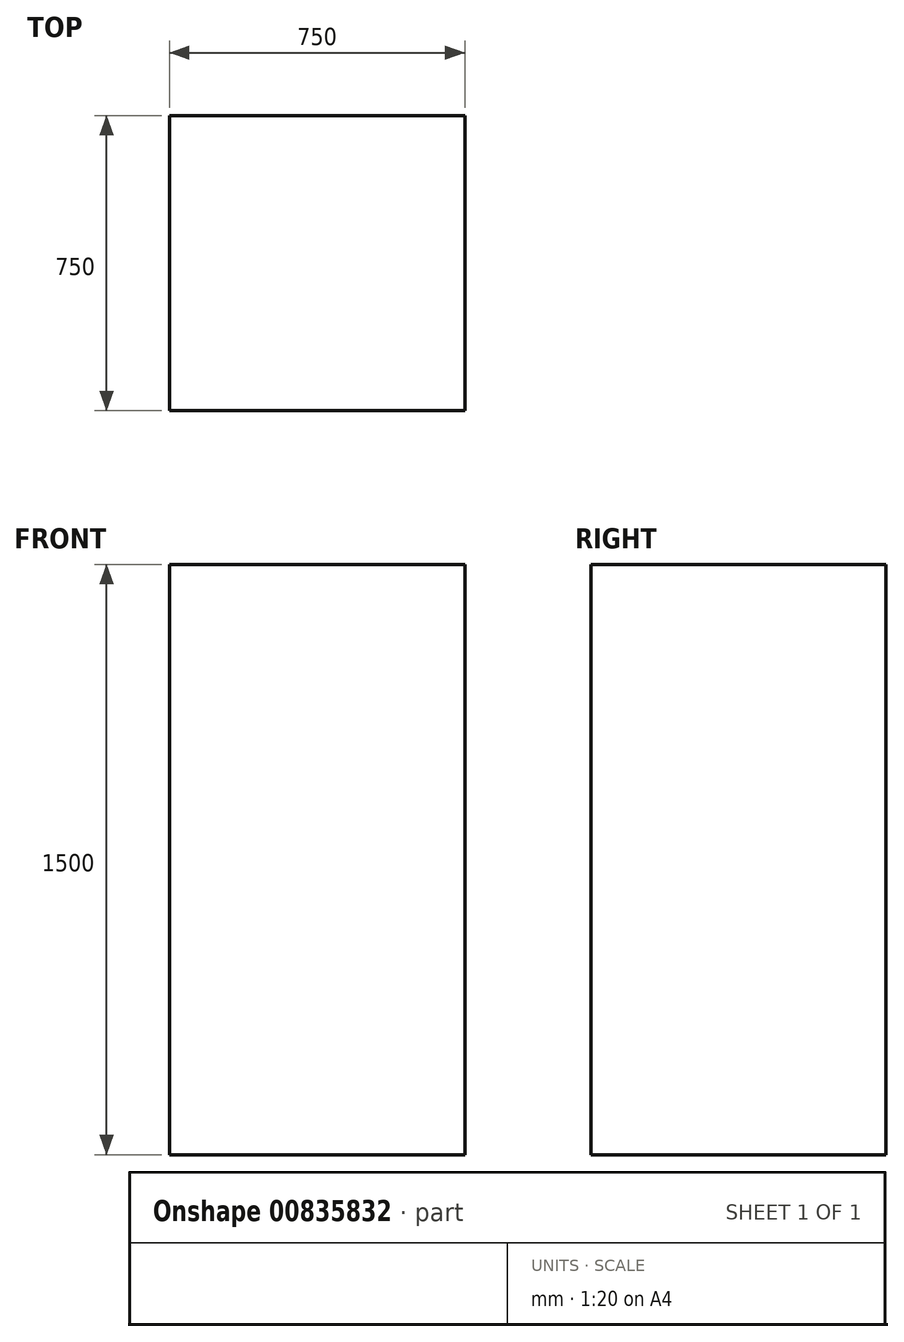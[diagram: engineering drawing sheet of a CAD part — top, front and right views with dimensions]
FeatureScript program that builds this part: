
annotation { "Feature Type Name" : "Feature", "Feature Type Description" : "" }
export const myFeature = defineFeature(function(context is Context, id is Id, definition is map)
    precondition{}
    {
        {
            var Q0;
            Q0=qCreatedBy(makeId("Top.planeOp"),FACE);
            var sketch = newSketch(context, id + "F0", { "sketchPlane" : qUnion([Q0])});
            skLineSegment(sketch, "E0.bottom", {"start": v(-375, 375) * mm, "end": v(375, 375) * mm});
            skLineSegment(sketch, "E0.top", {"start": v(-375, -375) * mm, "end": v(375, -375) * mm});
            skLineSegment(sketch, "E0.left", {"start": v(-375, 375) * mm, "end": v(-375, -375) * mm});
            skLineSegment(sketch, "E0.right", {"start": v(375, 375) * mm, "end": v(375, -375) * mm});
            skPoint(sketch, "E1", {"position": v(0, 375) * mm});
            skPoint(sketch, "E2", {"position": v(-375, 0) * mm});
            skSolve(sketch);
        }
        {
            var Q0;
            Q0=makeQuery(id+"F0.imprint","IMPRINT",FACE,{"disambiguationData":[TD([[makeQuery(id+"F0.imprint","IMPRINT",EDGE,{"derivedFrom":sQuery(id+"F0.wireOp",EDGE,"E0.bottom")}),-1.0]])]});
            extrude(context, id + "F1", {"entities" : qUnion([Q0]), "depth" : 1500 * mm, "offsetDistance" : 25.4 * mm});
        }
    });
